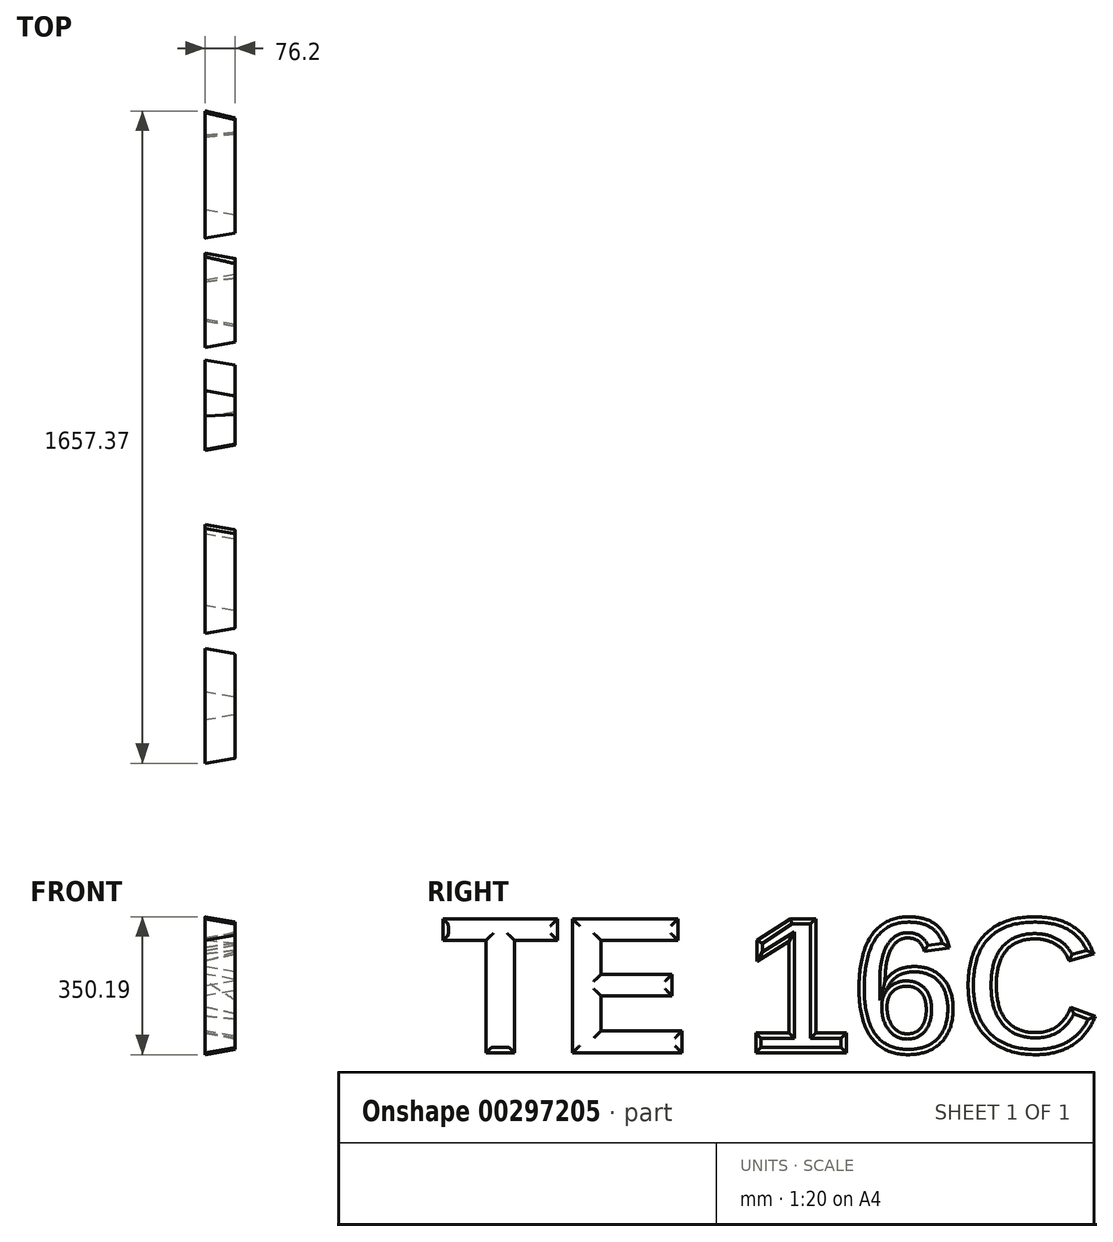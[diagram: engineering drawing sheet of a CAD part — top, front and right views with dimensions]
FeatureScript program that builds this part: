
annotation { "Feature Type Name" : "Feature", "Feature Type Description" : "" }
export const myFeature = defineFeature(function(context is Context, id is Id, definition is map)
    precondition{}
    {
        {
            var Q0;
            Q0=qCreatedBy(makeId("Right.planeOp"),FACE);
            var sketch = newSketch(context, id + "F0", { "sketchPlane" : qUnion([Q0])});
            skText(sketch, "E0", { "text": "TE 16C", "fontName": "Arimo-Bold.ttf"});
            const initialGuessF0  = {"E0": [-0.02784, -0.1797, 1, 0, 0.35606]};
            skSetInitialGuess(sketch, initialGuessF0);
            skSolve(sketch);
        }
        {
            var Q0;
            Q0 = qSketchRegion(id + "F0", true);
            extrude(context, id + "F1", {"entities" : qUnion([Q0]), "depth" : 76.2 * mm, "hasDraft" : true, "draftAngle" : 10 * degree, "draftPullDirection" : true});
        }
        {
            var Q0;
            Q0=makeQuery(id+"F1.opExtrude","CAP_EDGE",EDGE,{"disambiguationData":[OSD([sQuery(id+"F0.wireOp",EDGE,"E0.sketch_text.stroke-0")])],"isStart":false});
            var Q1;
            Q1=makeQuery(id+"F1.opExtrude","CAP_EDGE",EDGE,{"disambiguationData":[OSD([sQuery(id+"F0.wireOp",EDGE,"E0.sketch_text.stroke-5")])],"isStart":false});
            var Q2;
            Q2=makeQuery(id+"F1.opExtrude","CAP_EDGE",EDGE,{"disambiguationData":[OSD([sQuery(id+"F0.wireOp",EDGE,"E0.sketch_text.stroke-7")])],"isStart":false});
            var Q3;
            Q3=makeQuery(id+"F1.opExtrude","CAP_EDGE",EDGE,{"disambiguationData":[OSD([sQuery(id+"F0.wireOp",EDGE,"E0.sketch_text.stroke-6")])],"isStart":false});
            var Q4;
            Q4=makeQuery(id+"F1.opExtrude","CAP_EDGE",EDGE,{"disambiguationData":[OSD([sQuery(id+"F0.wireOp",EDGE,"E0.sketch_text.stroke-2")])],"isStart":false});
            var Q5;
            Q5=makeQuery(id+"F1.opExtrude","CAP_EDGE",EDGE,{"disambiguationData":[OSD([sQuery(id+"F0.wireOp",EDGE,"E0.sketch_text.stroke-3")])],"isStart":false});
            var Q6;
            Q6=makeQuery(id+"F1.opExtrude","CAP_EDGE",EDGE,{"disambiguationData":[OSD([sQuery(id+"F0.wireOp",EDGE,"E0.sketch_text.stroke-8")])],"isStart":false});
            var Q7;
            Q7=makeQuery(id+"F1.opExtrude","CAP_EDGE",EDGE,{"disambiguationData":[OSD([sQuery(id+"F0.wireOp",EDGE,"E0.sketch_text.stroke-9")])],"isStart":false});
            var Q8;
            Q8=makeQuery(id+"F1.opExtrude","CAP_EDGE",EDGE,{"disambiguationData":[OSD([sQuery(id+"F0.wireOp",EDGE,"E0.sketch_text.stroke-12")])],"isStart":false});
            var Q9;
            Q9=makeQuery(id+"F1.opExtrude","CAP_EDGE",EDGE,{"disambiguationData":[OSD([sQuery(id+"F0.wireOp",EDGE,"E0.sketch_text.stroke-11")])],"isStart":false});
            var Q10;
            Q10=makeQuery(id+"F1.opExtrude","CAP_EDGE",EDGE,{"disambiguationData":[OSD([sQuery(id+"F0.wireOp",EDGE,"E0.sketch_text.stroke-15")])],"isStart":false});
            var Q11;
            Q11=makeQuery(id+"F1.opExtrude","CAP_EDGE",EDGE,{"disambiguationData":[OSD([sQuery(id+"F0.wireOp",EDGE,"E0.sketch_text.stroke-13")])],"isStart":false});
            var Q12;
            Q12=makeQuery(id+"F1.opExtrude","CAP_EDGE",EDGE,{"disambiguationData":[OSD([sQuery(id+"F0.wireOp",EDGE,"E0.sketch_text.stroke-14")])],"isStart":false});
            var Q13;
            Q13=makeQuery(id+"F1.opExtrude","CAP_EDGE",EDGE,{"disambiguationData":[OSD([sQuery(id+"F0.wireOp",EDGE,"E0.sketch_text.stroke-10")])],"isStart":false});
            var Q14;
            Q14=makeQuery(id+"F1.opExtrude","CAP_EDGE",EDGE,{"disambiguationData":[OSD([sQuery(id+"F0.wireOp",EDGE,"E0.sketch_text.stroke-16")])],"isStart":false});
            var Q15;
            Q15=makeQuery(id+"F1.opExtrude","CAP_EDGE",EDGE,{"disambiguationData":[OSD([sQuery(id+"F0.wireOp",EDGE,"E0.sketch_text.stroke-17")])],"isStart":false});
            var Q16;
            Q16=makeQuery(id+"F1.opExtrude","CAP_EDGE",EDGE,{"disambiguationData":[OSD([sQuery(id+"F0.wireOp",EDGE,"E0.sketch_text.stroke-18")])],"isStart":false});
            var Q17;
            Q17=makeQuery(id+"F1.opExtrude","CAP_EDGE",EDGE,{"disambiguationData":[OSD([sQuery(id+"F0.wireOp",EDGE,"E0.sketch_text.stroke-19")])],"isStart":false});
            fillet(context, id + "F2", {"entities" : qUnion([Q0, Q1, Q2, Q3, Q4, Q5, Q6, Q7, Q8, Q9, Q10, Q11, Q12, Q13, Q14, Q15, Q16, Q17]), "radius" : 5.08 * mm, "tangentPropagation" : true, "allowEdgeOverflow" : false});
        }
    });
